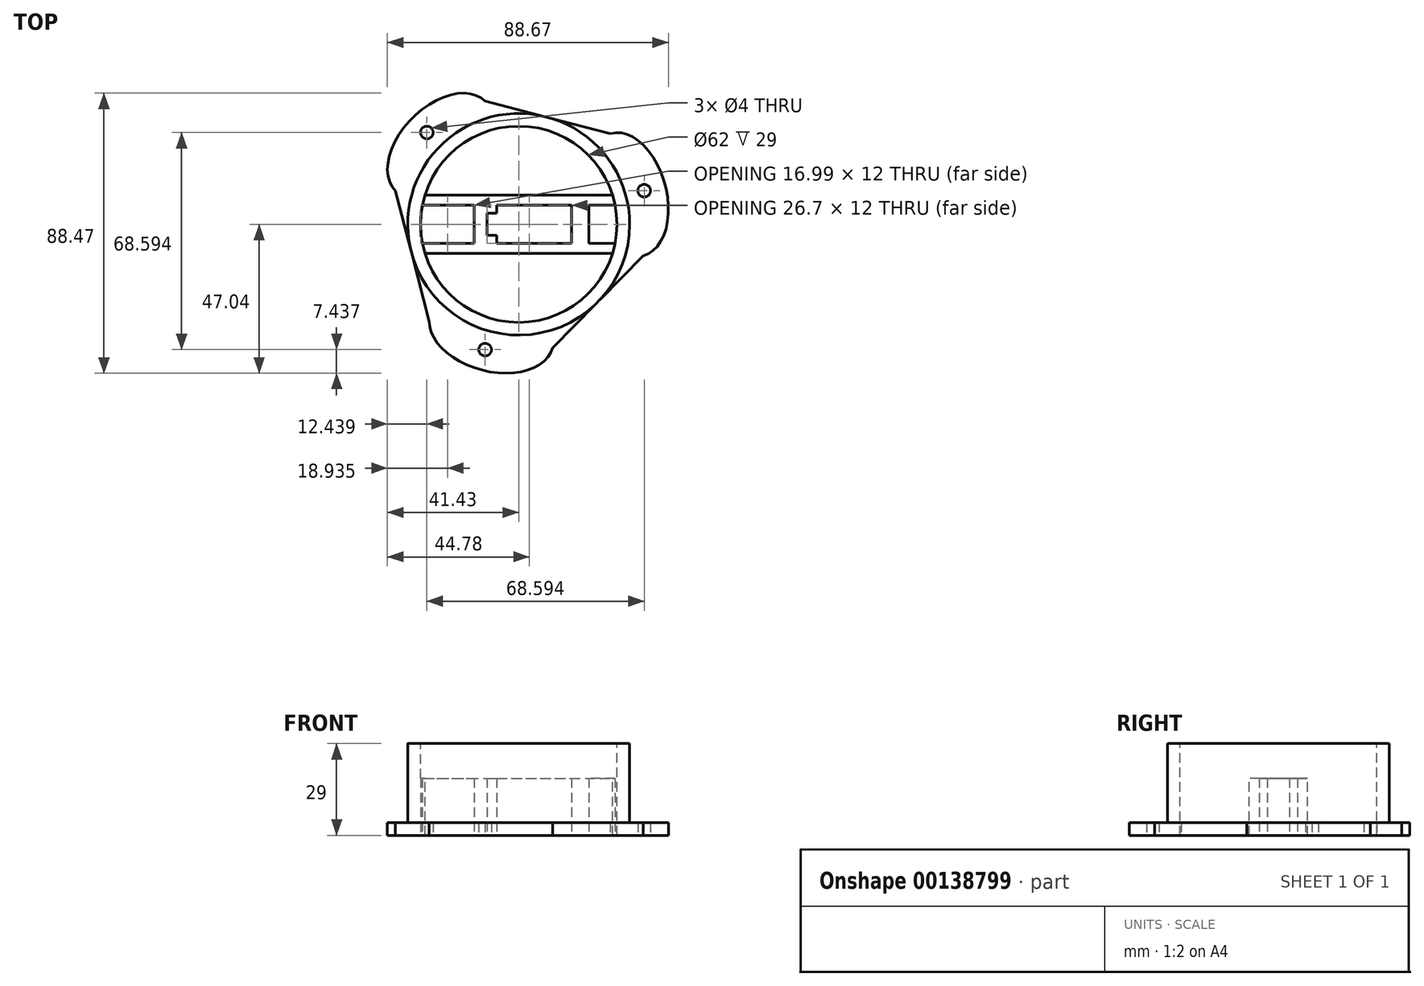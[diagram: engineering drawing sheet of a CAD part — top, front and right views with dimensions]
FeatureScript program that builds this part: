
annotation { "Feature Type Name" : "Feature", "Feature Type Description" : "" }
export const myFeature = defineFeature(function(context is Context, id is Id, definition is map)
    precondition{}
    {
        {
            var Q0;
            Q0=qCreatedBy(makeId("Top.planeOp"),FACE);
            var sketch = newSketch(context, id + "F0", { "sketchPlane" : qUnion([Q0])});
            skCircle(sketch, "E0", {"center": v(0, 0) * mm, "radius": 35 * mm, "construction": true});
            skLineSegment(sketch, "E1", {"start": v(0, 0) * mm, "end": v(-53.68, 53.68) * mm, "construction": true});
            skLineSegment(sketch, "E2", {"start": v(-24.75, 24.75) * mm, "end": v(-10.6, 38.9) * mm, "construction": true});
            skPoint(sketch, "E2.endSnap0", {"position": v(-10.6, 38.9) * mm});
            skPoint(sketch, "E3.center", {"position": v(0.24, 0.08) * mm});
            skLineSegment(sketch, "E4", {"start": v(-10.6, 38.9) * mm, "end": v(28.93, 28.7) * mm});
            skLineSegment(sketch, "E5", {"start": v(39.28, -9.93) * mm, "end": v(10.7, -39.08) * mm});
            skLineSegment(sketch, "E6", {"start": v(-38.9, 10.6) * mm, "end": v(-28.21, -30.72) * mm});
            skLineSegment(sketch, "E7", {"start": v(10.7, -39.08) * mm, "end": v(-8.62, -33.9) * mm, "construction": true});
            skEllipticalArc(sketch, "E8", {});
            skEllipticalArc(sketch, "E9", {"construction": true});
            skEllipticalArc(sketch, "E10", {"construction": true});
            skEllipticalArc(sketch, "E11", {});
            skEllipticalArc(sketch, "E12", {});
            skEllipticalArc(sketch, "E13", {"construction": true});
            skCircle(sketch, "E14", {"center": v(-29, 29) * mm, "radius": 2 * mm});
            skCircle(sketch, "E15.1.0", {"center": v(-10.61, -39.6) * mm, "radius": 2 * mm});
            skCircle(sketch, "E15.2.0", {"center": v(39.6, 10.61) * mm, "radius": 2 * mm});
            const initialGuessF0  = {"E8": [-0.024748737341529173, 0.02474873734152916, 0.7071067811865474, 0.7071067811865478, 0.02, 0.0125, 0, 3.141592653589793], "E9": [-0.024748737341529173, 0.02474873734152916, 0.7071067811865474, 0.7071067811865478, 0.02, 0.0125, 3.141592653589793, 0], "E10": [0.03410784128529934, 0.00938656512054002, 0.2588190451025208, -0.9659258262890683, 0.02, 0.0125, 3.141592653589793, 0], "E11": [0.03410784128529934, 0.00938656512054002, 0.2588190451025208, -0.9659258262890683, 0.02, 0.0125, 0, 3.141592653589793], "E12": [-0.008624479428803128, -0.0339036410396351, -0.9659258262890682, 0.25881904510252096, 0.02, 0.0125, 0.16001835229444727, 3.141592653589793], "E13": [-0.008624479428803128, -0.0339036410396351, -0.9659258262890682, 0.25881904510252096, 0.02, 0.0125, 3.141592653589793, 0.16001835229444727]};
            skSetInitialGuess(sketch, initialGuessF0);
            skSolve(sketch);
        }
        {
            var Q0;
            Q0=makeQuery(id+"F0.imprint","IMPRINT",FACE,{"disambiguationData":[TD([[makeQuery(id+"F0.imprint","IMPRINT",EDGE,{"derivedFrom":sQuery(id+"F0.wireOp",EDGE,"E4")}),-1.0]])]});
            var Q1;
            Q1=sQuery(id+"F0.wireOp",EDGE,"E4");
            var Q2;
            Q2=sQuery(id+"F0.wireOp",EDGE,"E8");
            var Q3;
            Q3=sQuery(id+"F0.wireOp",EDGE,"E6");
            var Q4;
            Q4=sQuery(id+"F0.wireOp",EDGE,"E12");
            var Q5;
            Q5=sQuery(id+"F0.wireOp",EDGE,"E5");
            var Q6;
            Q6=sQuery(id+"F0.wireOp",EDGE,"E11");
            extrude(context, id + "F1", {"entities" : qUnion([Q0]), "surfaceEntities" : qUnion([Q1, Q2, Q3, Q4, Q5, Q6]), "depth" : 4 * mm});
        }
        {
            var Q0;
            Q0=makeQuery(id+"F1.opExtrude","CAP_FACE",FACE,{"disambiguationData":[OSD([sQuery(id+"F0.wireOp",EDGE,"E4"),sQuery(id+"F0.wireOp",EDGE,"E5"),sQuery(id+"F0.wireOp",EDGE,"E6"),sQuery(id+"F0.wireOp",EDGE,"E8"),sQuery(id+"F0.wireOp",EDGE,"E11"),sQuery(id+"F0.wireOp",EDGE,"E12")])],"isStart":false});
            var sketch = newSketch(context, id + "F2", { "sketchPlane" : qUnion([Q0])});
            skCircle(sketch, "E16", {"center": v(0, 0) * mm, "radius": 35.02 * mm});
            skSolve(sketch);
        }
        {
            var Q0;
            Q0=qSketchRegion(id+"F2",true);
            extrude(context, id + "F3", {"entities" : qUnion([Q0]), "operationType" : NewBodyOperationType.ADD, "depth" : 25 * mm});
        }
        {
            var Q0;
            Q0=makeQuery(id+"F3.opExtrude","CAP_FACE",FACE,{"disambiguationData":[OSD([sQuery(id+"F2.wireOp",EDGE,"E16")])],"isStart":false});
            var sketch = newSketch(context, id + "F4", { "sketchPlane" : qUnion([Q0])});
            skCircle(sketch, "E17", {"center": v(0, 0) * mm, "radius": 31 * mm});
            skSolve(sketch);
        }
        {
            var Q0;
            Q0=makeQuery(id+"F4.imprint","IMPRINT",FACE,{"disambiguationData":[TD([[makeQuery(id+"F4.imprint","IMPRINT",EDGE,{"derivedFrom":sQuery(id+"F4.wireOp",EDGE,"E17")}),1.0]])]});
            extrude(context, id + "F5", {"entities" : qUnion([Q0]), "operationType" : NewBodyOperationType.REMOVE, "endBound" : BoundingType.THROUGH_ALL, "oppositeDirection" : true, "depth" : 25 * mm});
        }
        {
            var Q0;
            Q0=qCreatedBy(makeId("Top.planeOp"),FACE);
            var sketch = newSketch(context, id + "F6", { "sketchPlane" : qUnion([Q0])});
            skLineSegment(sketch, "E18.bottom", {"start": v(-31.5, 9.25) * mm, "end": v(31.5, 9.25) * mm});
            skLineSegment(sketch, "E18.top", {"start": v(-31.5, -9.25) * mm, "end": v(31.5, -9.25) * mm});
            skLineSegment(sketch, "E18.left", {"start": v(-31.5, 9.25) * mm, "end": v(-31.5, -9.25) * mm});
            skLineSegment(sketch, "E18.right", {"start": v(31.5, 9.25) * mm, "end": v(31.5, -9.25) * mm});
            skPoint(sketch, "E18.middle", {"position": v(0, 0) * mm});
            skSolve(sketch);
        }
        {
            var Q0;
            Q0=makeQuery(id+"F6.imprint","IMPRINT",FACE,{"disambiguationData":[TD([[makeQuery(id+"F6.imprint","IMPRINT",EDGE,{"derivedFrom":sQuery(id+"F6.wireOp",EDGE,"E18.bottom")}),-1.0]])]});
            extrude(context, id + "F7", {"entities" : qUnion([Q0]), "operationType" : NewBodyOperationType.ADD, "depth" : 18 * mm});
        }
        {
            var Q0;
            Q0=qCreatedBy(makeId("Top.planeOp"),FACE);
            var sketch = newSketch(context, id + "F8", { "sketchPlane" : qUnion([Q0])});
            skLineSegment(sketch, "E19.bottom", {"start": v(31.5, 9.25) * mm, "end": v(-31.5, 9.25) * mm});
            skLineSegment(sketch, "E19.top", {"start": v(31.5, -9.25) * mm, "end": v(-31.5, -9.25) * mm});
            skLineSegment(sketch, "E19.left", {"start": v(31.5, 9.25) * mm, "end": v(31.5, -9.25) * mm, "construction": true});
            skLineSegment(sketch, "E19.right", {"start": v(-31.5, 9.25) * mm, "end": v(-31.5, -9.25) * mm, "construction": true});
            skPoint(sketch, "E19.middle", {"position": v(0, 0) * mm});
            skLineSegment(sketch, "E20.bottom", {"start": v(-14, 6) * mm, "end": v(-30.4, 6) * mm});
            skLineSegment(sketch, "E20.top", {"start": v(-14, -6) * mm, "end": v(-32, -6) * mm});
            skLineSegment(sketch, "E20.left", {"start": v(-14, 6) * mm, "end": v(-14, -6) * mm});
            skPoint(sketch, "E20.middle", {"position": v(-23, 0) * mm});
            skLineSegment(sketch, "E21.bottom", {"start": v(16.7, 6) * mm, "end": v(-7, 6) * mm});
            skLineSegment(sketch, "E21.top", {"start": v(16.7, -6) * mm, "end": v(-7, -6) * mm});
            skLineSegment(sketch, "E21.left", {"start": v(16.7, 6) * mm, "end": v(16.7, -6) * mm});
            skLineSegment(sketch, "E21.right", {"start": v(-7, 6) * mm, "end": v(-7, 3.5) * mm});
            skPoint(sketch, "E21.middle", {"position": v(4.85, 0) * mm});
            skLineSegment(sketch, "E22.bottom", {"start": v(-7, 3.5) * mm, "end": v(-10, 3.5) * mm});
            skLineSegment(sketch, "E22.top", {"start": v(-7, -3.5) * mm, "end": v(-10, -3.5) * mm});
            skLineSegment(sketch, "E22.left", {"start": v(-7, 3.5) * mm, "end": v(-7, -3.5) * mm, "construction": true});
            skLineSegment(sketch, "E22.right", {"start": v(-10, 3.5) * mm, "end": v(-10, -3.5) * mm});
            skPoint(sketch, "E22.middle", {"position": v(-8.5, 0) * mm});
            skPoint(sketch, "E22.middle.positionSnap0", {"position": v(-7, 0) * mm});
            skPoint(sketch, "E22.centerSnap0", {"position": v(-7, 0) * mm});
            skLineSegment(sketch, "E23", {"start": v(-7, -3.5) * mm, "end": v(-7, -6) * mm});
            skLineSegment(sketch, "E24.bottom", {"start": v(22.2, 6) * mm, "end": v(30.41, 6) * mm});
            skLineSegment(sketch, "E24.top", {"start": v(22.2, -6) * mm, "end": v(32.33, -6) * mm});
            skLineSegment(sketch, "E24.left", {"start": v(22.2, 6) * mm, "end": v(22.2, -6) * mm});
            skLineSegment(sketch, "E24.right", {"start": v(32.33, 6) * mm, "end": v(32.33, -6) * mm, "construction": true});
            skPoint(sketch, "E24.middle", {"position": v(27.27, 0) * mm});
            skLineSegment(sketch, "E25", {"start": v(30.41, 6) * mm, "end": v(32.33, 6) * mm, "construction": true});
            skArc(sketch, "E26", {"start": v(30.41, -6) * mm, "mid": v(31, 0) * mm, "end": v(30.41, 6) * mm});
            skLineSegment(sketch, "E27", {"start": v(-31.5, 6) * mm, "end": v(-32, 6) * mm});
            skArc(sketch, "E28", {"start": v(-30.41, -6) * mm, "mid": v(-30.04, -7.64) * mm, "end": v(-29.59, -9.25) * mm});
            skArc(sketch, "E29", {"start": v(-30.4, 6) * mm, "mid": v(-31, 0) * mm, "end": v(-30.41, -6) * mm});
            skArc(sketch, "E30.trimOffspring", {"start": v(-29.59, 9.25) * mm, "mid": v(-30.03, 7.64) * mm, "end": v(-30.4, 6) * mm});
            skArc(sketch, "E31.trimOffspring", {"start": v(29.59, -9.25) * mm, "mid": v(30.04, -7.64) * mm, "end": v(30.41, -6) * mm});
            skSolve(sketch);
        }
        {
            var Q0;
            Q0=qSketchRegion(id+"F8",true);
            extrude(context, id + "F9", {"entities" : qUnion([Q0]), "operationType" : NewBodyOperationType.REMOVE, "endBound" : BoundingType.THROUGH_ALL, "depth" : 25 * mm});
        }
    });
